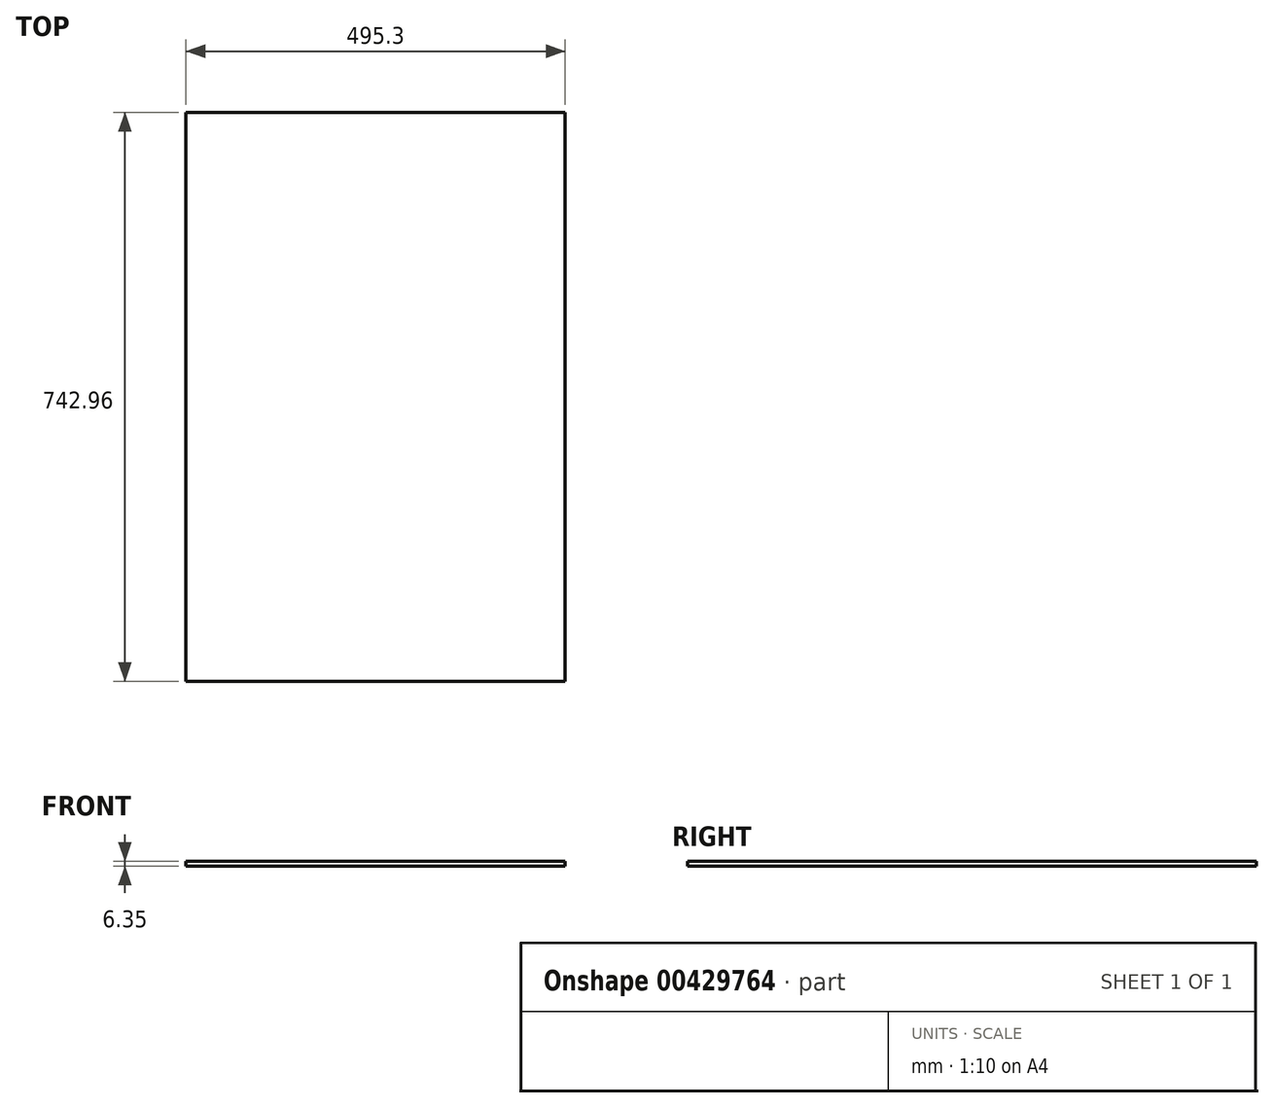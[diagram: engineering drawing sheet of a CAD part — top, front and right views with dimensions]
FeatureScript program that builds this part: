
annotation { "Feature Type Name" : "Feature", "Feature Type Description" : "" }
export const myFeature = defineFeature(function(context is Context, id is Id, definition is map)
    precondition{}
    {
        {
            var Q0;
            Q0=qCreatedBy(makeId("Top.planeOp"),FACE);
            var sketch = newSketch(context, id + "F0", { "sketchPlane" : qUnion([Q0])});
            skLineSegment(sketch, "E0.bottom", {"start": v(-247.65, 371.48) * mm, "end": v(247.65, 371.48) * mm});
            skLineSegment(sketch, "E0.top", {"start": v(-247.65, -371.48) * mm, "end": v(247.65, -371.48) * mm});
            skLineSegment(sketch, "E0.left", {"start": v(-247.65, 371.48) * mm, "end": v(-247.65, -371.48) * mm});
            skLineSegment(sketch, "E0.right", {"start": v(247.65, 371.48) * mm, "end": v(247.65, -371.48) * mm});
            skPoint(sketch, "E0.middle", {"position": v(0, 0) * mm});
            skSolve(sketch);
        }
        {
            var Q0;
            Q0 = qSketchRegion(id + "F0", true);
            extrude(context, id + "F1", {"entities" : qUnion([Q0]), "depth" : 6.35 * mm});
        }
    });
